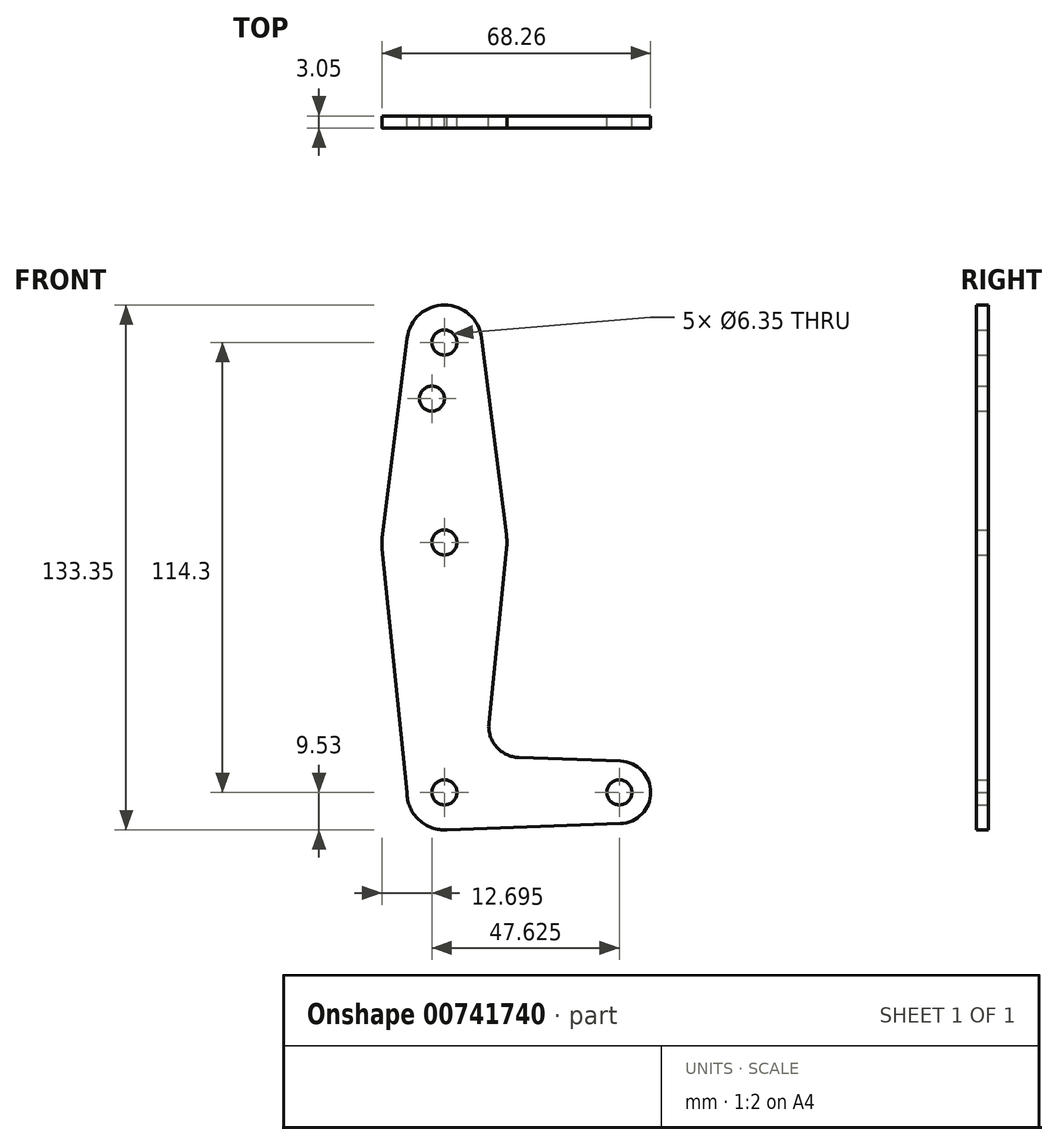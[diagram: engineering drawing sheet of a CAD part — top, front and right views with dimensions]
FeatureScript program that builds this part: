
annotation { "Feature Type Name" : "Feature", "Feature Type Description" : "" }
export const myFeature = defineFeature(function(context is Context, id is Id, definition is map)
    precondition{}
    {
        {
            var Q0;
            Q0=qCreatedBy(makeId("Front.planeOp"),FACE);
            var sketch = newSketch(context, id + "F0", { "sketchPlane" : qUnion([Q0])});
            skLineSegment(sketch, "E0", {"start": v(0, 50.8) * mm, "end": v(0, -63.5) * mm, "construction": true});
            skCircle(sketch, "E1", {"center": v(0, 50.8) * mm, "radius": 9.53 * mm});
            skCircle(sketch, "E2", {"center": v(0, 0) * mm, "radius": 15.88 * mm});
            skCircle(sketch, "E3", {"center": v(0, -63.5) * mm, "radius": 9.53 * mm});
            skLineSegment(sketch, "E4", {"start": v(0, -63.5) * mm, "end": v(44.45, -63.5) * mm, "construction": true});
            skCircle(sketch, "E5", {"center": v(44.45, -63.5) * mm, "radius": 7.94 * mm});
            skLineSegment(sketch, "E6", {"start": v(9.45, 52) * mm, "end": v(16, 0) * mm});
            skLineSegment(sketch, "E7", {"start": v(-9.45, 52) * mm, "end": v(-16, 0) * mm});
            skLineSegment(sketch, "E8", {"start": v(11.3, -45.9) * mm, "end": v(15.8, -1.6) * mm});
            skLineSegment(sketch, "E9", {"start": v(-9.52, -63.5) * mm, "end": v(-15.8, -1.6) * mm});
            skPoint(sketch, "E9.startSnap0", {"position": v(22.23, -63.5) * mm});
            skLineSegment(sketch, "E10", {"start": v(18.93, -54.65) * mm, "end": v(44.73, -55.57) * mm});
            skLineSegment(sketch, "E11", {"start": v(0, -73.03) * mm, "end": v(44.73, -71.43) * mm});
            skCircle(sketch, "E12", {"center": v(0, 50.8) * mm, "radius": 3.18 * mm});
            skCircle(sketch, "E13", {"center": v(0, 0) * mm, "radius": 3.18 * mm});
            skCircle(sketch, "E14", {"center": v(0, -63.5) * mm, "radius": 3.18 * mm});
            skCircle(sketch, "E15", {"center": v(44.45, -63.5) * mm, "radius": 3.18 * mm});
            skCircle(sketch, "E16", {"center": v(-3.17, 36.53) * mm, "radius": 3.18 * mm});
            skArc(sketch, "E17.filletArc", {"start": v(11.3, -45.9) * mm, "mid": v(13.22, -51.93) * mm, "end": v(18.93, -54.65) * mm});
            skSolve(sketch);
        }
        {
            var Q0;
            Q0 = qSketchRegion(id + "F0", true);
            extrude(context, id + "F1", {"entities" : qUnion([Q0]), "depth" : 3.05 * mm, "offsetDistance" : 25.4 * mm});
        }
    });
